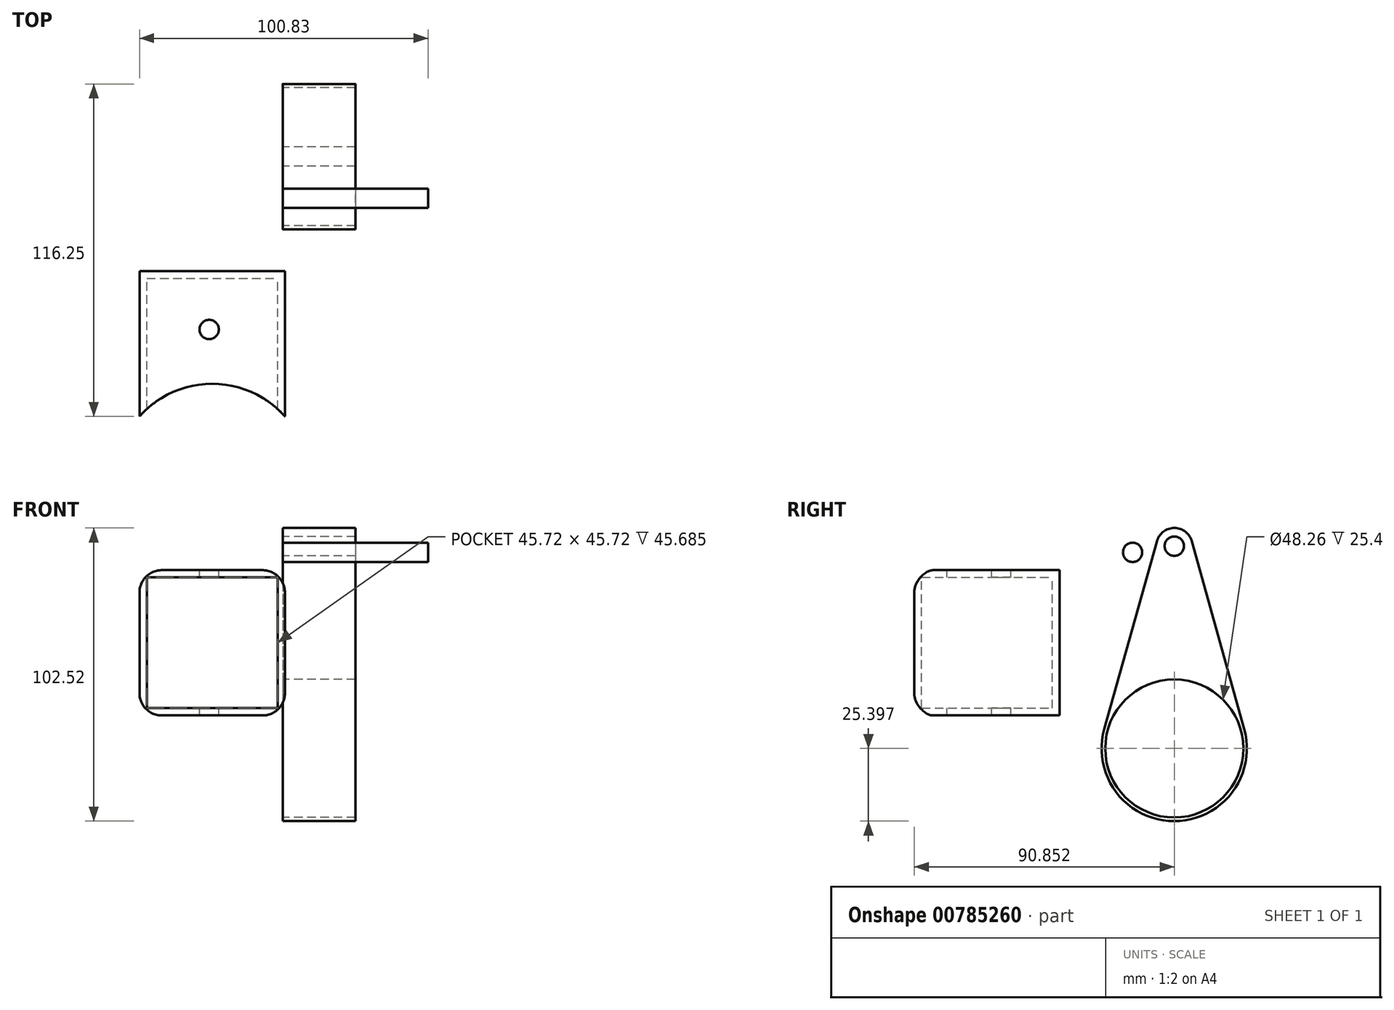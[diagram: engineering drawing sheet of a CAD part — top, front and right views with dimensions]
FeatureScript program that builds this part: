
annotation { "Feature Type Name" : "Feature", "Feature Type Description" : "" }
export const myFeature = defineFeature(function(context is Context, id is Id, definition is map)
    precondition{}
    {
        {
            var Q0;
            Q0=qCreatedBy(makeId("Front.planeOp"),FACE);
            var sketch = newSketch(context, id + "F0", { "sketchPlane" : qUnion([Q0])});
            skLineSegment(sketch, "E0.bottom", {"start": v(-50.03, -24.37) * mm, "end": v(0.77, -24.37) * mm});
            skLineSegment(sketch, "E0.top", {"start": v(-50.03, 26.43) * mm, "end": v(0.77, 26.43) * mm});
            skLineSegment(sketch, "E0.left", {"start": v(-50.03, -24.37) * mm, "end": v(-50.03, 26.43) * mm});
            skLineSegment(sketch, "E0.right", {"start": v(0.77, -24.37) * mm, "end": v(0.77, 26.43) * mm});
            skSolve(sketch);
        }
        {
            var Q0;
            Q0=makeQuery(id+"F0.imprint","IMPRINT",FACE,{"disambiguationData":[TD([[makeQuery(id+"F0.imprint","IMPRINT",EDGE,{"derivedFrom":sQuery(id+"F0.wireOp",EDGE,"E0.bottom")}),1.0]])]});
            extrude(context, id + "F1", {"entities" : qUnion([Q0]), "depth" : 50.8 * mm, "offsetDistance" : 25.4 * mm});
        }
        {
            var Q0;
            Q0=makeQuery(id+"F1.opExtrude","CAP_FACE",FACE,{"disambiguationData":[OSD([sQuery(id+"F0.wireOp",EDGE,"E0.bottom"),sQuery(id+"F0.wireOp",EDGE,"E0.top"),sQuery(id+"F0.wireOp",EDGE,"E0.left"),sQuery(id+"F0.wireOp",EDGE,"E0.right")])],"isStart":false});
            shell(context, id + "F2", {"entities" : qUnion([Q0]), "thickness" : 2.54 * mm});
        }
        {
            var Q0;
            Q0=makeQuery(id+"F1.opExtrude","SWEPT_FACE",FACE,{"disambiguationData":[OSD([sQuery(id+"F0.wireOp",EDGE,"E0.top")])]});
            var sketch = newSketch(context, id + "F3", { "sketchPlane" : qUnion([Q0])});
            skArc(sketch, "E1", {"start": v(0.77, -50.8) * mm, "mid": v(-24.63, -39.37) * mm, "end": v(-50.03, -50.8) * mm});
            skCircle(sketch, "E2", {"center": v(-25.68, -20.4) * mm, "radius": 3.38 * mm});
            skCircle(sketch, "E3", {"center": v(-25.68, -20.4) * mm, "radius": 7.62 * mm});
            skSolve(sketch);
        }
        {
            var Q0;
            Q0=makeQuery(id+"F3.imprint","IMPRINT",FACE,{"disambiguationData":[TD([[makeQuery(id+"F3.imprint","IMPRINT",EDGE,{"derivedFrom":sQuery(id+"F3.wireOp",EDGE,"E1")}),1.0]])]});
            var Q1;
            Q1=makeQuery(id+"F3.imprint","IMPRINT",FACE,{"disambiguationData":[TD([[makeQuery(id+"F3.imprint","IMPRINT",EDGE,{"derivedFrom":sQuery(id+"F3.wireOp",EDGE,"E2")}),1.0]])]});
            extrude(context, id + "F4", {"entities" : qUnion([Q0, Q1]), "operationType" : NewBodyOperationType.REMOVE, "oppositeDirection" : true, "depth" : 52.83 * mm, "offsetDistance" : 25.4 * mm});
        }
        {
            var Q0;
            Q0=makeQuery(id+"F1.opExtrude","SWEPT_EDGE",EDGE,{"disambiguationData":[OSD([sQuery(id+"F0.wireOp",EDGE,"E0.bottom"),sQuery(id+"F0.wireOp",EDGE,"E0.right")])]});
            var Q1;
            Q1=makeQuery(id+"F1.opExtrude","SWEPT_EDGE",EDGE,{"disambiguationData":[OSD([sQuery(id+"F0.wireOp",EDGE,"E0.bottom"),sQuery(id+"F0.wireOp",EDGE,"E0.left")])]});
            var Q2;
            Q2=makeQuery(id+"F1.opExtrude","SWEPT_EDGE",EDGE,{"disambiguationData":[OSD([sQuery(id+"F0.wireOp",EDGE,"E0.top"),sQuery(id+"F0.wireOp",EDGE,"E0.right")])]});
            var Q3;
            Q3=makeQuery(id+"F1.opExtrude","SWEPT_EDGE",EDGE,{"disambiguationData":[OSD([sQuery(id+"F0.wireOp",EDGE,"E0.top"),sQuery(id+"F0.wireOp",EDGE,"E0.left")])]});
            fillet(context, id + "F5", {"entities" : qUnion([Q0, Q1, Q2, Q3]), "radius" : 7.62 * mm, "tangentPropagation" : true, "rho" : .4, "crossSection" : FilletCrossSection.CONIC, "allowEdgeOverflow" : false});
        }
        {
            var Q0;
            Q0=qCreatedBy(makeId("Right.planeOp"),FACE);
            var sketch = newSketch(context, id + "F6", { "sketchPlane" : qUnion([Q0])});
            skCircle(sketch, "E4", {"center": v(40.08, 34.85) * mm, "radius": 6.35 * mm});
            skCircle(sketch, "E5", {"center": v(40.05, -35.92) * mm, "radius": 25.4 * mm});
            skLineSegment(sketch, "E6", {"start": v(33.97, 36.56) * mm, "end": v(15.6, -29.08) * mm});
            skLineSegment(sketch, "E7", {"start": v(46.2, 36.56) * mm, "end": v(64.52, -29.1) * mm});
            skSolve(sketch);
        }
        {
            var Q0;
            {var subQ0=sQuery(id+"F6.wireOp",EDGE,"E6");Q0=makeQuery(id+"F6.imprint","IMPRINT",FACE,{"disambiguationData":[TD([[makeQuery(id+"F6.imprint","IMPRINT",EDGE,{"derivedFrom":subQ0}),1.0]])]});}
            var Q1;
            {var subQ0=sQuery(id+"F6.wireOp",EDGE,"E4");var subQ1=makeQuery(id+"F6.imprint","INTERSECT",VERTEX,{"derivedFrom":[subQ0,sQuery(id+"F6.wireOp",EDGE,"E6")]});Q1=makeQuery(id+"F6.imprint","IMPRINT",FACE,{"disambiguationData":[TD([[makeQuery(id+"F6.imprint","IMPRINT",EDGE,{"disambiguationData":[TD([[subQ1,1.0]])],"derivedFrom":subQ0}),1.0]])]});}
            var Q2;
            {var subQ0=sQuery(id+"F6.wireOp",EDGE,"E5");var subQ1=makeQuery(id+"F6.imprint","INTERSECT",VERTEX,{"derivedFrom":[subQ0,sQuery(id+"F6.wireOp",EDGE,"E6")]});Q2=makeQuery(id+"F6.imprint","IMPRINT",FACE,{"disambiguationData":[TD([[makeQuery(id+"F6.imprint","IMPRINT",EDGE,{"disambiguationData":[TD([[subQ1,1.0]])],"derivedFrom":subQ0}),1.0]])]});}
            extrude(context, id + "F7", {"entities" : qUnion([Q0, Q1, Q2]), "depth" : 25.4 * mm, "offsetDistance" : 25.4 * mm});
        }
        {
            var Q0;
            Q0=sQuery(id+"F6.wireOp",VERTEX,"E4.center");
            var Q1;
            Q1=makeQuery(id+"F7.opExtrude","SWEPT_BODY",BODY,{"disambiguationData":[OSD([sQuery(id+"F6.wireOp",EDGE,"E4"),sQuery(id+"F6.wireOp",EDGE,"E5"),sQuery(id+"F6.wireOp",EDGE,"E6"),sQuery(id+"F6.wireOp",EDGE,"E7")])]});
            hole(context, id + "F8", {"style" : HoleStyle.SIMPLE, "endStyle" : HoleEndStyle.BLIND, "oppositeDirection" : true, "standardTappedOrClearance" : lookupTablePath({ "standard" : "ANSI", "fit" : "Normal (ASME)", "size" : "1/4", "type" : "Clearance" }), "standardBlindInLast" : lookupTablePath({ "fit" : "Free", "standard" : "ANSI", "size" : "1/4", "type" : "Clearance" }), "holeDiameter" : 6.76 * mm, "majorDiameter" : 6.35 * mm, "holeDepth" : 25.4 * mm, "isTappedThrough" : true, "tappedDepth" : 12.7 * mm, "tapClearance" : 3, "locations" : qUnion([Q0]), "scope" : qUnion([Q1])});
        }
        {
            var Q0;
            Q0=sQuery(id+"F6.wireOp",VERTEX,"E5.center");
            var Q1;
            Q1=makeQuery(id+"F7.opExtrude","SWEPT_BODY",BODY,{"disambiguationData":[OSD([sQuery(id+"F6.wireOp",EDGE,"E4"),sQuery(id+"F6.wireOp",EDGE,"E5"),sQuery(id+"F6.wireOp",EDGE,"E6"),sQuery(id+"F6.wireOp",EDGE,"E7")])]});
            hole(context, id + "F9", {"style" : HoleStyle.SIMPLE, "endStyle" : HoleEndStyle.BLIND, "oppositeDirection" : true, "holeDiameter" : 48.26 * mm, "majorDiameter" : 6.35 * mm, "holeDepth" : 50.8 * mm, "isTappedThrough" : true, "tappedDepth" : 12.7 * mm, "tapClearance" : 3, "locations" : qUnion([Q0]), "scope" : qUnion([Q1])});
        }
        {
            var Q0;
            Q0=qCreatedBy(makeId("Right.planeOp"),FACE);
            var sketch = newSketch(context, id + "F10", { "sketchPlane" : qUnion([Q0])});
            skCircle(sketch, "E8", {"center": v(25.5, 32.68) * mm, "radius": 3.37 * mm});
            skSolve(sketch);
        }
        {
            var Q0;
            Q0=makeQuery(id+"F10.imprint","IMPRINT",FACE,{"disambiguationData":[TD([[makeQuery(id+"F10.imprint","IMPRINT",EDGE,{"derivedFrom":sQuery(id+"F10.wireOp",EDGE,"E8")}),1.0]])]});
            extrude(context, id + "F11", {"entities" : qUnion([Q0]), "depth" : 50.8 * mm, "offsetDistance" : 25.4 * mm});
        }
    });
